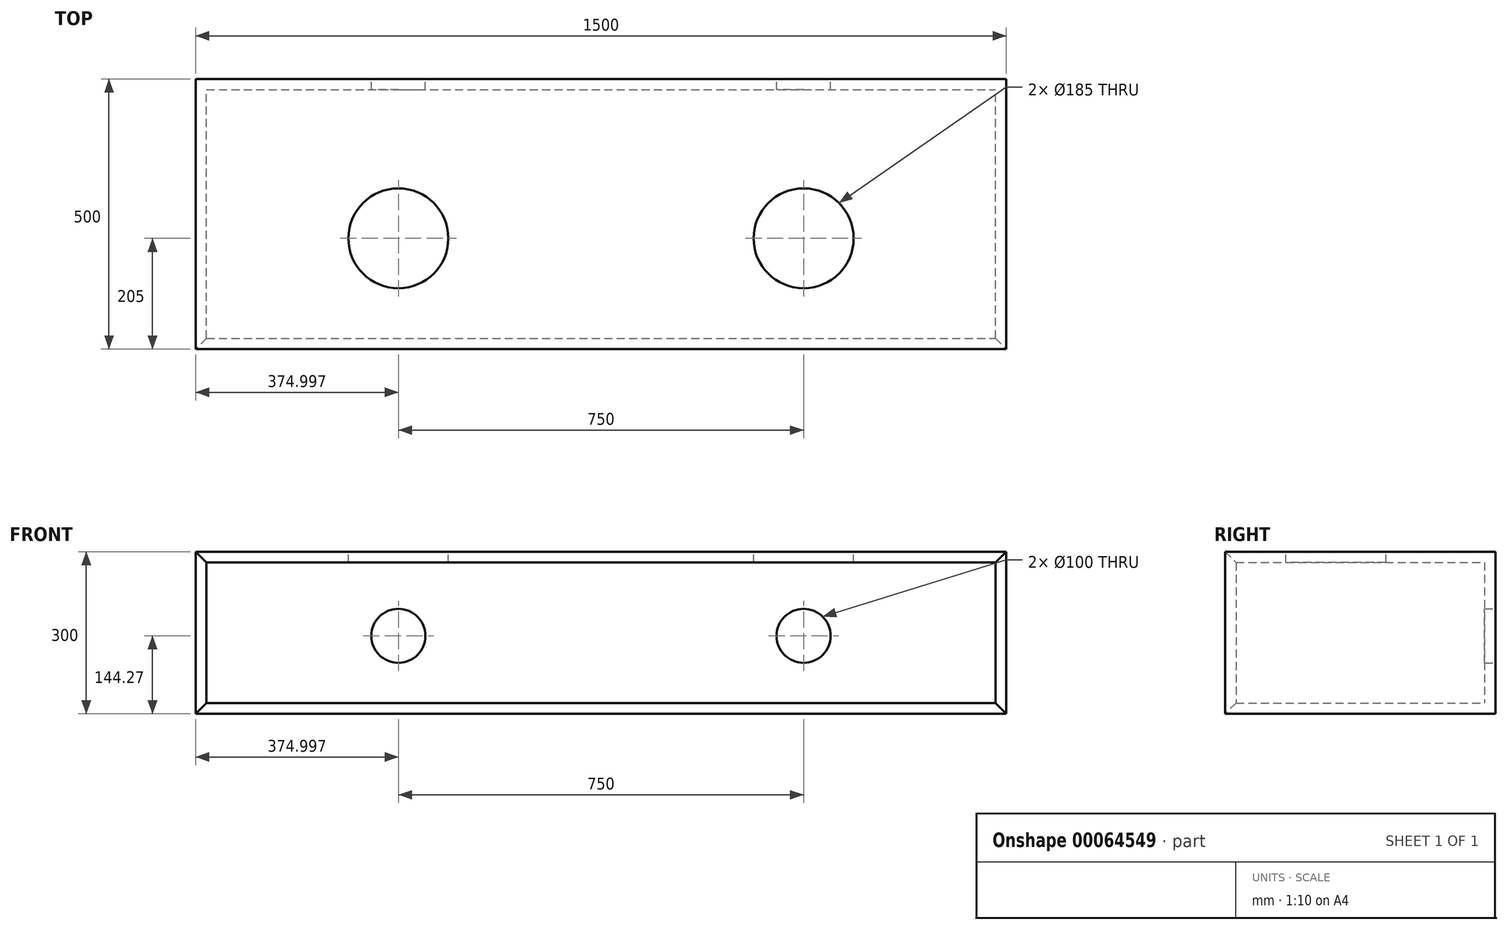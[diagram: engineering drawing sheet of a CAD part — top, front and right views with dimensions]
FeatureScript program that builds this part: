
annotation { "Feature Type Name" : "Feature", "Feature Type Description" : "" }
export const myFeature = defineFeature(function(context is Context, id is Id, definition is map)
    precondition{}
    {
        {
            var Q0;
            Q0=qCreatedBy(makeId("Front.planeOp"),FACE);
            var sketch = newSketch(context, id + "F0", { "sketchPlane" : qUnion([Q0])});
            skLineSegment(sketch, "E0.bottom", {"start": v(-735.18, 155.73) * mm, "end": v(764.82, 155.73) * mm});
            skLineSegment(sketch, "E0.top", {"start": v(-735.18, -144.27) * mm, "end": v(764.82, -144.27) * mm});
            skLineSegment(sketch, "E0.left", {"start": v(-735.18, 155.73) * mm, "end": v(-735.18, -144.27) * mm});
            skLineSegment(sketch, "E0.right", {"start": v(764.82, 155.73) * mm, "end": v(764.82, -144.27) * mm});
            skSolve(sketch);
        }
        {
            var Q0;
            Q0=makeQuery(id+"F0.imprint","IMPRINT",FACE,{"disambiguationData":[TD([[makeQuery(id+"F0.imprint","IMPRINT",EDGE,{"derivedFrom":sQuery(id+"F0.wireOp",EDGE,"E0.bottom")}),-1.0]])]});
            extrude(context, id + "F1", {"entities" : qUnion([Q0]), "depth" : 480 * mm});
        }
        {
            var Q0;
            Q0=makeQuery(id+"F1.opExtrude","CAP_FACE",FACE,{"disambiguationData":[OSD([sQuery(id+"F0.wireOp",EDGE,"E0.bottom"),sQuery(id+"F0.wireOp",EDGE,"E0.top"),sQuery(id+"F0.wireOp",EDGE,"E0.left"),sQuery(id+"F0.wireOp",EDGE,"E0.right")])],"isStart":false});
            shell(context, id + "F2", {"entities" : qUnion([Q0]), "thickness" : 20 * mm});
        }
        {
            var Q0;
            Q0=makeQuery(id+"F1.opExtrude","CAP_FACE",FACE,{"disambiguationData":[OSD([sQuery(id+"F0.wireOp",EDGE,"E0.bottom"),sQuery(id+"F0.wireOp",EDGE,"E0.top"),sQuery(id+"F0.wireOp",EDGE,"E0.left"),sQuery(id+"F0.wireOp",EDGE,"E0.right")])],"isStart":false});
            extrude(context, id + "F3", {"entities" : qUnion([Q0]), "depth" : 20 * mm});
        }
        {
            var Q0;
            {var subQ0=sQuery(id+"F0.wireOp",EDGE,"E0.top");Q0=makeQuery(id+"F3.opExtrude","CAP_EDGE",EDGE,{"disambiguationData":[OSD([subQ0]),TDD([makeQuery(id+"F2.opShell","OFFSET_EDGE",EDGE,{"disambiguationData":[OSD([subQ0]),TDD([makeQuery(id+"F1.opExtrude","CAP_EDGE",EDGE,{"disambiguationData":[OSD([subQ0])],"isStart":false})])]})])],"isStart":false});}
            var Q1;
            {var subQ0=sQuery(id+"F0.wireOp",EDGE,"E0.right");Q1=makeQuery(id+"F3.opExtrude","CAP_EDGE",EDGE,{"disambiguationData":[OSD([subQ0]),TDD([makeQuery(id+"F2.opShell","OFFSET_EDGE",EDGE,{"disambiguationData":[OSD([subQ0]),TDD([makeQuery(id+"F1.opExtrude","CAP_EDGE",EDGE,{"disambiguationData":[OSD([subQ0])],"isStart":false})])]})])],"isStart":false});}
            var Q2;
            {var subQ0=sQuery(id+"F0.wireOp",EDGE,"E0.left");Q2=makeQuery(id+"F3.opExtrude","CAP_EDGE",EDGE,{"disambiguationData":[OSD([subQ0]),TDD([makeQuery(id+"F2.opShell","OFFSET_EDGE",EDGE,{"disambiguationData":[OSD([subQ0]),TDD([makeQuery(id+"F1.opExtrude","CAP_EDGE",EDGE,{"disambiguationData":[OSD([subQ0])],"isStart":false})])]})])],"isStart":false});}
            var Q3;
            {var subQ0=sQuery(id+"F0.wireOp",EDGE,"E0.bottom");Q3=makeQuery(id+"F3.opExtrude","CAP_EDGE",EDGE,{"disambiguationData":[OSD([subQ0]),TDD([makeQuery(id+"F2.opShell","OFFSET_EDGE",EDGE,{"disambiguationData":[OSD([subQ0]),TDD([makeQuery(id+"F1.opExtrude","CAP_EDGE",EDGE,{"disambiguationData":[OSD([subQ0])],"isStart":false})])]})])],"isStart":false});}
            chamfer(context, id + "F4", {"entities" : qUnion([Q0, Q1, Q2, Q3]), "width" : 20 * mm, "tangentPropagation" : true});
        }
        {
            var Q0;
            Q0=makeQuery(id+"F1.opExtrude","SWEPT_BODY",BODY,{"disambiguationData":[OSD([sQuery(id+"F0.wireOp",EDGE,"E0.bottom"),sQuery(id+"F0.wireOp",EDGE,"E0.top"),sQuery(id+"F0.wireOp",EDGE,"E0.left"),sQuery(id+"F0.wireOp",EDGE,"E0.right")])]});
            var Q1;
            Q1=makeQuery(id+"F3.opExtrude","SWEPT_BODY",BODY,{"disambiguationData":[OSD([sQuery(id+"F0.wireOp",EDGE,"E0.bottom"),sQuery(id+"F0.wireOp",EDGE,"E0.top"),sQuery(id+"F0.wireOp",EDGE,"E0.left"),sQuery(id+"F0.wireOp",EDGE,"E0.right")])]});
            booleanBodies(context, id + "F5", {"operationType" : BooleanOperationType.UNION, "tools" : qUnion([Q0, Q1])});
        }
        {
            var Q0;
            Q0=makeQuery(id+"F1.opExtrude","CAP_FACE",FACE,{"disambiguationData":[OSD([sQuery(id+"F0.wireOp",EDGE,"E0.bottom"),sQuery(id+"F0.wireOp",EDGE,"E0.top"),sQuery(id+"F0.wireOp",EDGE,"E0.left"),sQuery(id+"F0.wireOp",EDGE,"E0.right")])],"isStart":true});
            var sketch = newSketch(context, id + "F6", { "sketchPlane" : qUnion([Q0])});
            skPoint(sketch, "E1", {"position": v(-389.82, 0) * mm});
            skPoint(sketch, "E2", {"position": v(360.18, 0) * mm});
            skSolve(sketch);
        }
        {
            var Q0;
            Q0=sQuery(id+"F6.wireOp",VERTEX,"E1");
            var Q1;
            Q1=sQuery(id+"F6.wireOp",VERTEX,"E2");
            var Q2;
            Q2=makeQuery(id+"F1.opExtrude","SWEPT_BODY",BODY,{"disambiguationData":[OSD([sQuery(id+"F0.wireOp",EDGE,"E0.bottom"),sQuery(id+"F0.wireOp",EDGE,"E0.top"),sQuery(id+"F0.wireOp",EDGE,"E0.left"),sQuery(id+"F0.wireOp",EDGE,"E0.right")])]});
            hole(context, id + "F7", {"style" : HoleStyle.SIMPLE, "holeDiameter" : 100 * mm, "endStyle" : HoleEndStyle.THROUGH, "locations" : qUnion([Q0, Q1]), "scope" : qUnion([Q2])});
        }
        {
            var Q0;
            {var subQ0=sQuery(id+"F0.wireOp",EDGE,"E0.bottom");Q0=makeQuery(id+"F5.opBoolean","MERGE",FACE,{"derivedFrom":[makeQuery(id+"F1.opExtrude","SWEPT_FACE",FACE,{"disambiguationData":[OSD([subQ0])]}),makeQuery(id+"F3.opExtrude","SWEPT_FACE",FACE,{"disambiguationData":[OSD([subQ0]),TDD([makeQuery(id+"F1.opExtrude","CAP_EDGE",EDGE,{"disambiguationData":[OSD([subQ0])],"isStart":false})])]})]});}
            var sketch = newSketch(context, id + "F8", { "sketchPlane" : qUnion([Q0])});
            skPoint(sketch, "E3", {"position": v(-360.18, -295) * mm});
            skPoint(sketch, "E4", {"position": v(389.82, -295) * mm});
            skSolve(sketch);
        }
        {
            var Q0;
            Q0=sQuery(id+"F8.wireOp",VERTEX,"E4");
            var Q1;
            Q1=sQuery(id+"F8.wireOp",VERTEX,"E3");
            var Q2;
            Q2=makeQuery(id+"F1.opExtrude","SWEPT_BODY",BODY,{"disambiguationData":[OSD([sQuery(id+"F0.wireOp",EDGE,"E0.bottom"),sQuery(id+"F0.wireOp",EDGE,"E0.top"),sQuery(id+"F0.wireOp",EDGE,"E0.left"),sQuery(id+"F0.wireOp",EDGE,"E0.right")])]});
            hole(context, id + "F9", {"style" : HoleStyle.SIMPLE, "holeDiameter" : 185 * mm, "endStyle" : HoleEndStyle.BLIND, "holeDepth" : 20 * mm, "locations" : qUnion([Q0, Q1]), "scope" : qUnion([Q2])});
        }
    });
